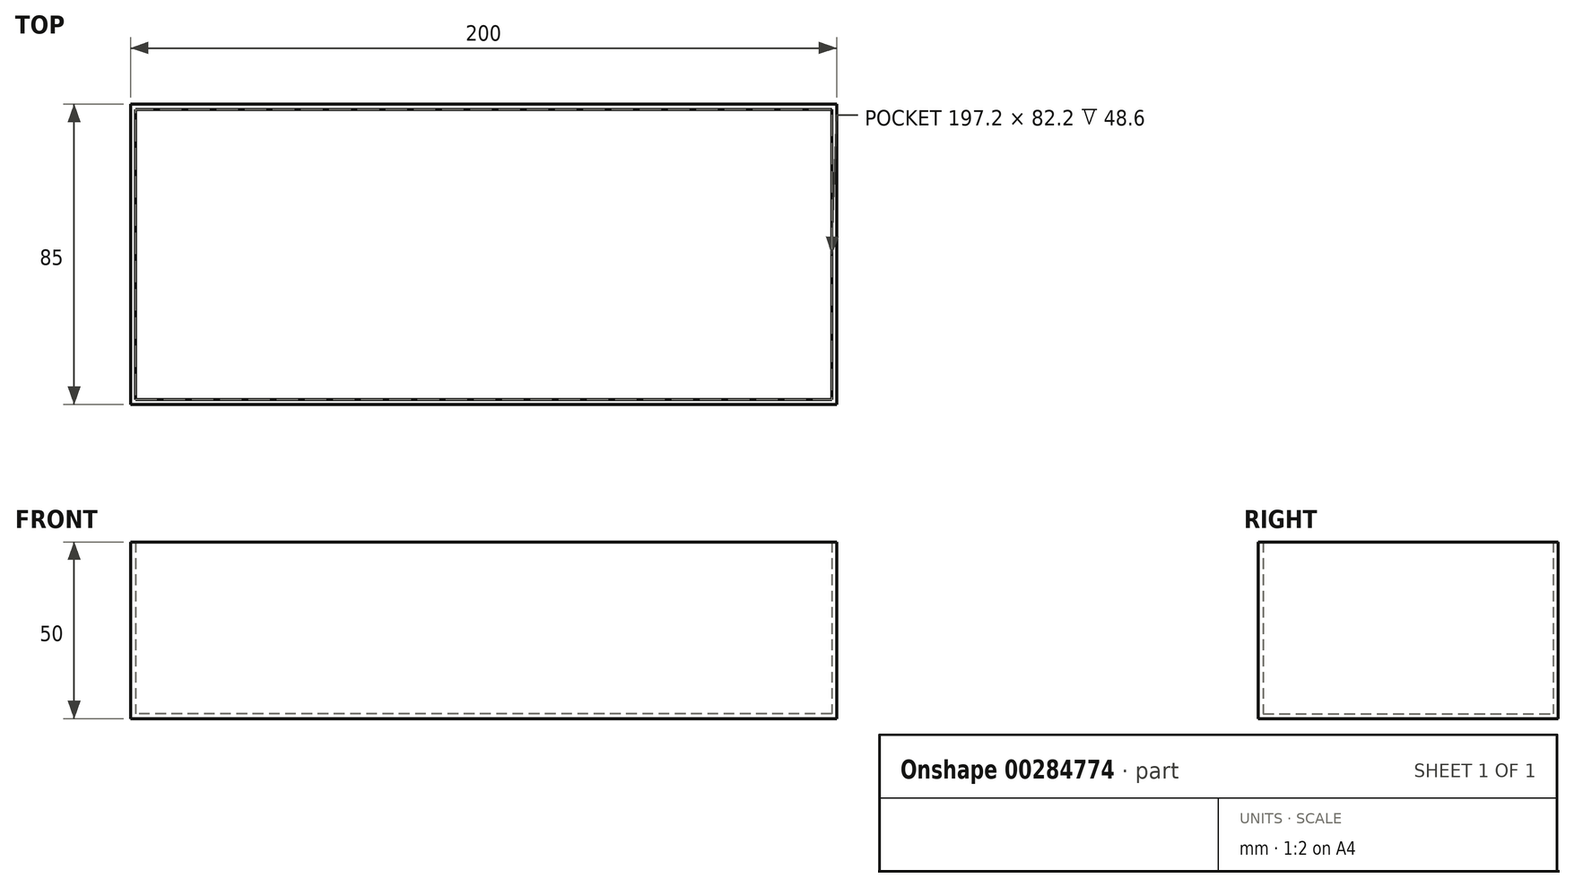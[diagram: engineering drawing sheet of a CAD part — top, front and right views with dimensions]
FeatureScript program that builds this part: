
annotation { "Feature Type Name" : "Feature", "Feature Type Description" : "" }
export const myFeature = defineFeature(function(context is Context, id is Id, definition is map)
    precondition{}
    {
        {
            var Q0;
            Q0=qCreatedBy(makeId("Top.planeOp"),FACE);
            var sketch = newSketch(context, id + "F0", { "sketchPlane" : qUnion([Q0])});
            skLineSegment(sketch, "E0.bottom", {"start": v(100, -42.5) * mm, "end": v(-100, -42.5) * mm});
            skLineSegment(sketch, "E0.top", {"start": v(100, 42.5) * mm, "end": v(-100, 42.5) * mm});
            skLineSegment(sketch, "E0.left", {"start": v(100, -42.5) * mm, "end": v(100, 42.5) * mm});
            skLineSegment(sketch, "E0.right", {"start": v(-100, -42.5) * mm, "end": v(-100, 42.5) * mm});
            skPoint(sketch, "E0.middle", {"position": v(0, 0) * mm});
            skSolve(sketch);
        }
        {
            var Q0;
            Q0 = qSketchRegion(id + "F0", true);
            extrude(context, id + "F1", {"entities" : qUnion([Q0]), "depth" : 50 * mm, "offsetDistance" : 25 * mm});
        }
        {
            var Q0;
            Q0=makeQuery(id+"F1.opExtrude","CAP_FACE",FACE,{"disambiguationData":[OSD([sQuery(id+"F0.wireOp",EDGE,"E0.bottom"),sQuery(id+"F0.wireOp",EDGE,"E0.top"),sQuery(id+"F0.wireOp",EDGE,"E0.left"),sQuery(id+"F0.wireOp",EDGE,"E0.right")])],"isStart":false});
            shell(context, id + "F2", {"entities" : qUnion([Q0]), "thickness" : 1.4 * mm});
        }
    });
